AUTODESK INVENTOR PART (.ipt)
format: ipt  version: 2021 (Build 250183000, 183)  size: 145,408 bytes
history: native  units: mm
features: chamfer x2, other x1, extrude x1, hole x1, fillet x1, sketch x1
ambient origin geometry x8: Origin, YZ Plane, XZ Plane, XY Plane, X Axis, Y Axis, Z Axis, Center Point
bodies: Body1 (feature_tree)
feature tree (7):
  other  "Sólido1"
  extrude  "Extrusión1"  Depth=1.0mm
  hole  "Agujero1"  [1 undecoded]
  fillet  "Empalme1"  Radius=8.0mm
  chamfer  "Chaflán1"  Distance=1.0mm
  chamfer  "Chaflán2"  Distance=1.0mm Angle=45.0deg
  sketch  "Boceto1"  dims[d1=60.0deg d2=17.0mm d3=60.0mm d5=360.0deg d7=8.0mm d8=0.0mm d9=10.0mm d10=10.0mm d11=22.376202mm d12=48.0mm d13=4.0mm d14=2.0mm d15=90.0deg d16=8.0mm d17=20.594885mm d18=1.0mm d19=1.0mm d20=2.0mm d21=45.0deg d22=1.0mm d23=2.0mm d24=45.0deg]
note: 1 required parameter value undecoded (feature->parameter linkage not recoverable at this tier; creation-order binding heuristic only, values carry confidence <= 0.55)
